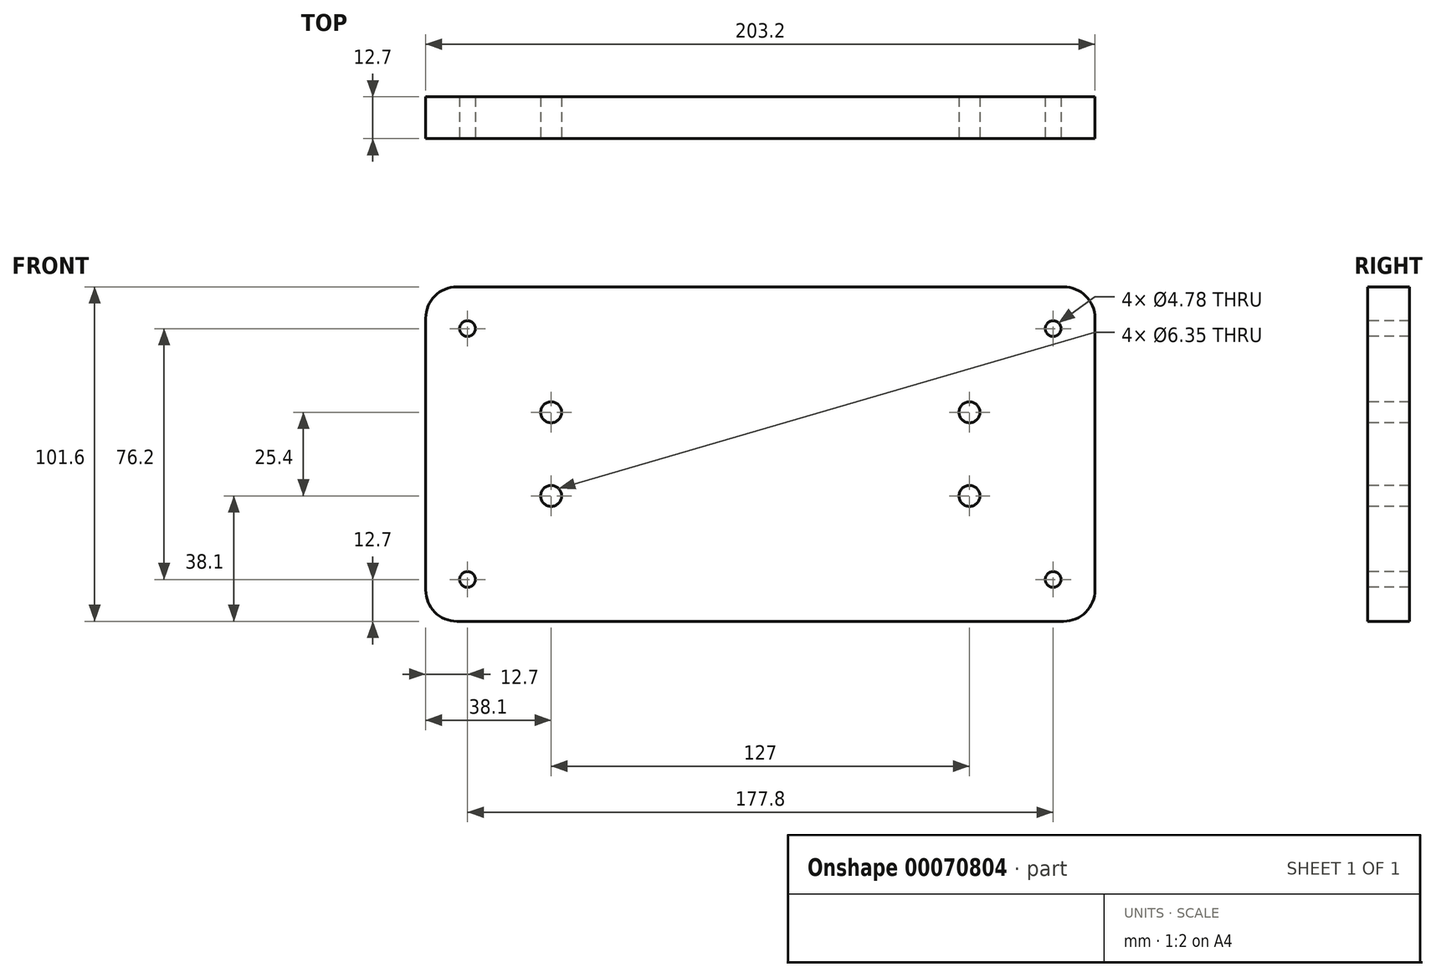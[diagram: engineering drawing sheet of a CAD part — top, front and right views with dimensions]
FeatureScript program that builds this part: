
annotation { "Feature Type Name" : "Feature", "Feature Type Description" : "" }
export const myFeature = defineFeature(function(context is Context, id is Id, definition is map)
    precondition{}
    {
        {
            var Q0;
            Q0=qCreatedBy(makeId("Front.planeOp"),FACE);
            var sketch = newSketch(context, id + "F0", { "sketchPlane" : qUnion([Q0])});
            skLineSegment(sketch, "E0.bottom", {"start": v(0, 0) * mm, "end": v(203.2, 0) * mm});
            skLineSegment(sketch, "E0.top", {"start": v(0, 101.6) * mm, "end": v(203.2, 101.6) * mm});
            skLineSegment(sketch, "E0.left", {"start": v(0, 0) * mm, "end": v(0, 101.6) * mm});
            skLineSegment(sketch, "E0.right", {"start": v(203.2, 0) * mm, "end": v(203.2, 101.6) * mm});
            skSolve(sketch);
        }
        {
            var Q0;
            Q0=makeQuery(id+"F0.imprint","IMPRINT",FACE,{"disambiguationData":[TD([[makeQuery(id+"F0.imprint","IMPRINT",EDGE,{"derivedFrom":sQuery(id+"F0.wireOp",EDGE,"E0.bottom")}),1.0]])]});
            extrude(context, id + "F1", {"entities" : qUnion([Q0]), "depth" : 12.7 * mm});
        }
        {
            var Q0;
            Q0=makeQuery(id+"F1.opExtrude","SWEPT_EDGE",EDGE,{"disambiguationData":[OSD([sQuery(id+"F0.wireOp",EDGE,"E0.top"),sQuery(id+"F0.wireOp",EDGE,"E0.left")])]});
            var Q1;
            Q1=makeQuery(id+"F1.opExtrude","SWEPT_EDGE",EDGE,{"disambiguationData":[OSD([sQuery(id+"F0.wireOp",EDGE,"E0.bottom"),sQuery(id+"F0.wireOp",EDGE,"E0.left")])]});
            var Q2;
            Q2=makeQuery(id+"F1.opExtrude","SWEPT_EDGE",EDGE,{"disambiguationData":[OSD([sQuery(id+"F0.wireOp",EDGE,"E0.bottom"),sQuery(id+"F0.wireOp",EDGE,"E0.right")])]});
            var Q3;
            Q3=makeQuery(id+"F1.opExtrude","SWEPT_EDGE",EDGE,{"disambiguationData":[OSD([sQuery(id+"F0.wireOp",EDGE,"E0.top"),sQuery(id+"F0.wireOp",EDGE,"E0.right")])]});
            fillet(context, id + "F2", {"entities" : qUnion([Q0, Q1, Q2, Q3]), "radius" : 9.52 * mm, "tangentPropagation" : true, "allowEdgeOverflow" : false});
        }
        {
            var Q0;
            Q0=makeQuery(id+"F1.opExtrude","CAP_FACE",FACE,{"disambiguationData":[OSD([sQuery(id+"F0.wireOp",EDGE,"E0.bottom"),sQuery(id+"F0.wireOp",EDGE,"E0.top"),sQuery(id+"F0.wireOp",EDGE,"E0.left"),sQuery(id+"F0.wireOp",EDGE,"E0.right")])],"isStart":false});
            var sketch = newSketch(context, id + "F3", { "sketchPlane" : qUnion([Q0])});
            skPoint(sketch, "E1", {"position": v(12.7, 88.9) * mm});
            skPoint(sketch, "E2", {"position": v(12.7, 12.7) * mm});
            skPoint(sketch, "E3", {"position": v(190.5, 12.7) * mm});
            skPoint(sketch, "E4", {"position": v(190.5, 88.9) * mm});
            skSolve(sketch);
        }
        {
            var Q0;
            Q0=sQuery(id+"F3.wireOp",VERTEX,"E2");
            var Q1;
            Q1=sQuery(id+"F3.wireOp",VERTEX,"E1");
            var Q2;
            Q2=sQuery(id+"F3.wireOp",VERTEX,"E4");
            var Q3;
            Q3=sQuery(id+"F3.wireOp",VERTEX,"E3");
            var Q4;
            Q4=makeQuery(id+"F1.opExtrude","SWEPT_BODY",BODY,{"disambiguationData":[OSD([sQuery(id+"F0.wireOp",EDGE,"E0.bottom"),sQuery(id+"F0.wireOp",EDGE,"E0.top"),sQuery(id+"F0.wireOp",EDGE,"E0.left"),sQuery(id+"F0.wireOp",EDGE,"E0.right")])]});
            hole(context, id + "F4", {"style" : HoleStyle.SIMPLE, "endStyle" : HoleEndStyle.THROUGH, "holeDiameter" : 4.78 * mm, "locations" : qUnion([Q0, Q1, Q2, Q3]), "scope" : qUnion([Q4]), "isTappedThrough" : true});
        }
        {
            var Q0;
            Q0=makeQuery(id+"F1.opExtrude","CAP_FACE",FACE,{"disambiguationData":[OSD([sQuery(id+"F0.wireOp",EDGE,"E0.bottom"),sQuery(id+"F0.wireOp",EDGE,"E0.top"),sQuery(id+"F0.wireOp",EDGE,"E0.left"),sQuery(id+"F0.wireOp",EDGE,"E0.right")])],"isStart":false});
            var sketch = newSketch(context, id + "F5", { "sketchPlane" : qUnion([Q0])});
            skPoint(sketch, "E5", {"position": v(38.1, 38.1) * mm});
            skPoint(sketch, "E6", {"position": v(38.1, 63.5) * mm});
            skPoint(sketch, "E7", {"position": v(165.1, 63.5) * mm});
            skPoint(sketch, "E8", {"position": v(165.1, 38.1) * mm});
            skSolve(sketch);
        }
        {
            var Q0;
            Q0=sQuery(id+"F5.wireOp",VERTEX,"E6");
            var Q1;
            Q1=sQuery(id+"F5.wireOp",VERTEX,"E5");
            var Q2;
            Q2=sQuery(id+"F5.wireOp",VERTEX,"E8");
            var Q3;
            Q3=sQuery(id+"F5.wireOp",VERTEX,"E7");
            var Q4;
            Q4=makeQuery(id+"F1.opExtrude","SWEPT_BODY",BODY,{"disambiguationData":[OSD([sQuery(id+"F0.wireOp",EDGE,"E0.bottom"),sQuery(id+"F0.wireOp",EDGE,"E0.top"),sQuery(id+"F0.wireOp",EDGE,"E0.left"),sQuery(id+"F0.wireOp",EDGE,"E0.right")])]});
            hole(context, id + "F6", {"style" : HoleStyle.SIMPLE, "endStyle" : HoleEndStyle.THROUGH, "holeDiameter" : 6.35 * mm, "locations" : qUnion([Q0, Q1, Q2, Q3]), "scope" : qUnion([Q4]), "isTappedThrough" : true});
        }
    });
